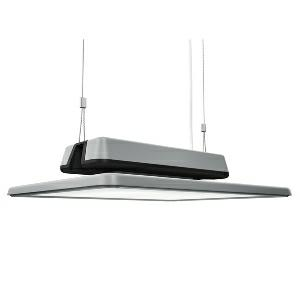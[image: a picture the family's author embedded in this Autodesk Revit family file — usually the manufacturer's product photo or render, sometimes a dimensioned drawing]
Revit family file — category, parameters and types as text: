
# Revit family: acaneo_-_hial_30000_840_n_dali_00732988_1371
name_source: partatom
category: Lighting Fixtures
units: mm (PartAtom-declared; Revit-internal decimal feet)

## family parameters
Cut with Voids When Loaded = No
Host = Face
Light Source = No
Part Type = Normal
Room Calculation Point = No
Round Connector Dimension = Use Diameter
Shared = No

## types (1)
- ACANEO - HIAL 30000/840/N/DALI (1 x LED, 33000 lm, 4000K)
    Apparent Load = 206 VA
    Approval mark = CE
    CIE Flux Codes = 84 97 100 100 100
    Color Rendering = 80-89
    Color Temperature = 4000K
    Control Gear = Electronic ballast
    Default Elevation = 1800 mm
    Description = HIAL 30000/840/N/DALI|High bay luminaire|light source: LED|work equipment: Adjustable electronic ballast, digital DALI|connected load: 220-240 V, 50/60 Hz|Power consumption: approx. 206 W|power factor: approx. 0,973|luminous flux: 33000 lm|luminous efficacy: 160 lm/W|colour temperature: Cold white, ca. 4000 K|color rendering index (CRI): >= 80|chromaticity tolerance:  3 SDCM|System of protection: IP 65|class of protection: I|technology: Continuously dimmable|luminaire body|material: Aluminium|surface: Powder coatet|colour: White aluminium|lamp cover: Acrylic (PMMA), Clear|weight (net): approx. 10.8 kg|mains lead: Built-in plug RST 20i5 Einbau|Fastening: Available separately|Accessory: Junction box (RST 20i5)|minimum ambient temperature: -30 ░C|maximum ambient temperature: 60 ░C|glare control: Optics|unified glare rating(4H 8H): <=  22|
    Frequency = 50 Hz, 60 Hz
    Height = 125 mm
    Lamp = 1 x LED
    Lamp Light Flux = 33000 lm
    Lamp count = 1
    Length = 585 mm
    Luminous efficacy = 160 lm/W
    Manufacturer = Waldmann
    ModVariant = No
    Model = 00732988
    Mounting Place = Ceiling
    Mounting Type = Pendant
    Number of Poles = 1
    OnlyDefault = Yes
    Power Factor = 1
    Product Name = ACANEO - HIAL 30000/840/N/DALI
    Product group = High bay luminaire (industry)
    ProductGroupID = 901
    Protection Class = Protection class I
    Protection Degree = IP 65
    RLX_Detail_Level = 1
    RLX_Emergency_Light_Flux = 0 lm
    RLX_Emergency_Type = 0
    RLX_Emergency_Type_DB = No
    RlxData = <blob elided: 29917 chars, md5=0acfaaf6>
    Socket = socket
    Standby Power = 0 W
    System Light Flux = 32999 lm
    System Power = 206 W
    Type Comments = Product without accessories
    Type Image = acaneo-hial.jpg
    URL = http://relux.com
    VarID = ---
    Voltage = 230 V
    Voltage Range = 110-120 V, 220-240 V
    Weight = 0.00 kg
    Width = 480 mm

## geometry (parser evidence)
native form markers: Blend x4, Sweep x10
no freeform markers — native parametric forms only
